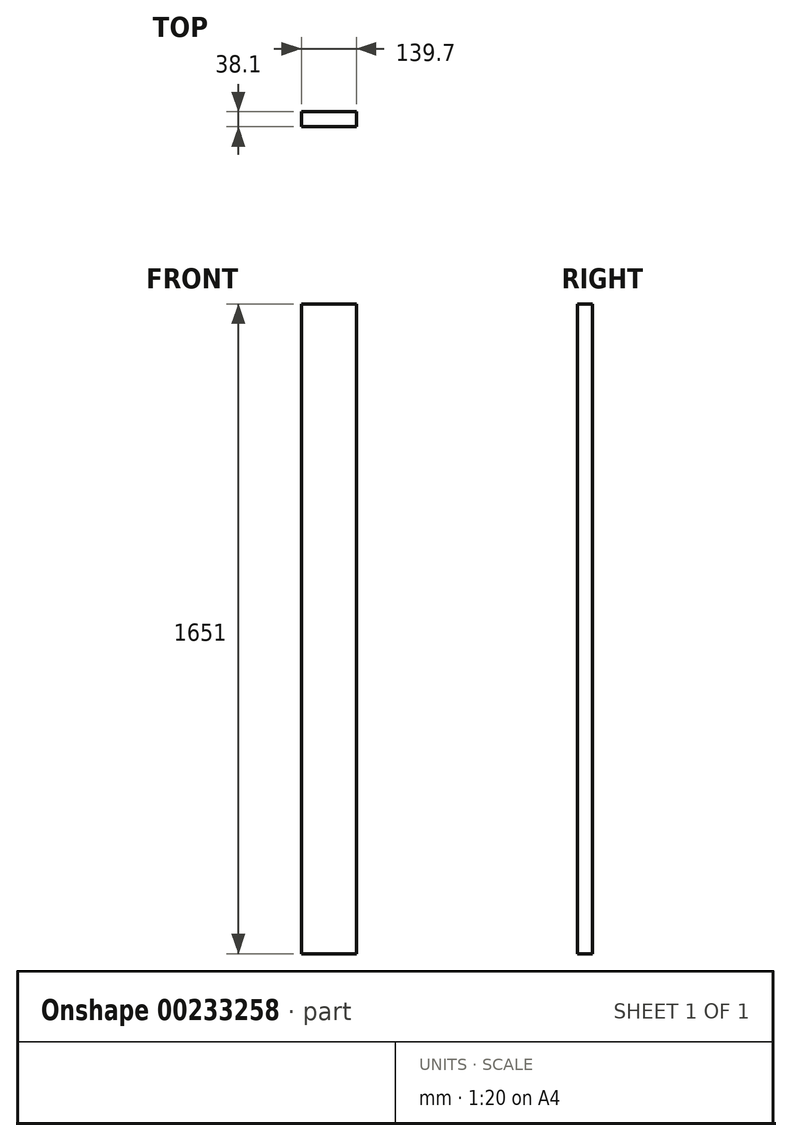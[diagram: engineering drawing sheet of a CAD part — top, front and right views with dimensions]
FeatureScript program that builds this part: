
annotation { "Feature Type Name" : "Feature", "Feature Type Description" : "" }
export const myFeature = defineFeature(function(context is Context, id is Id, definition is map)
    precondition{}
    {
        {
            var Q0;
            Q0=qCreatedBy(makeId("Front.planeOp"),FACE);
            var sketch = newSketch(context, id + "F0", { "sketchPlane" : qUnion([Q0])});
            skLineSegment(sketch, "E0", {"start": v(-128.93, 745.56) * mm, "end": v(-128.93, -905.44) * mm});
            skLineSegment(sketch, "E1", {"start": v(-128.93, -905.44) * mm, "end": v(10.77, -905.44) * mm});
            skLineSegment(sketch, "E2", {"start": v(10.77, -905.44) * mm, "end": v(10.77, 745.56) * mm});
            skLineSegment(sketch, "E3", {"start": v(10.77, 745.56) * mm, "end": v(-128.93, 745.56) * mm});
            skSolve(sketch);
        }
        {
            var Q0;
            Q0 = qSketchRegion(id + "F0", true);
            extrude(context, id + "F1", {"entities" : qUnion([Q0]), "depth" : 38.1 * mm});
        }
    });
